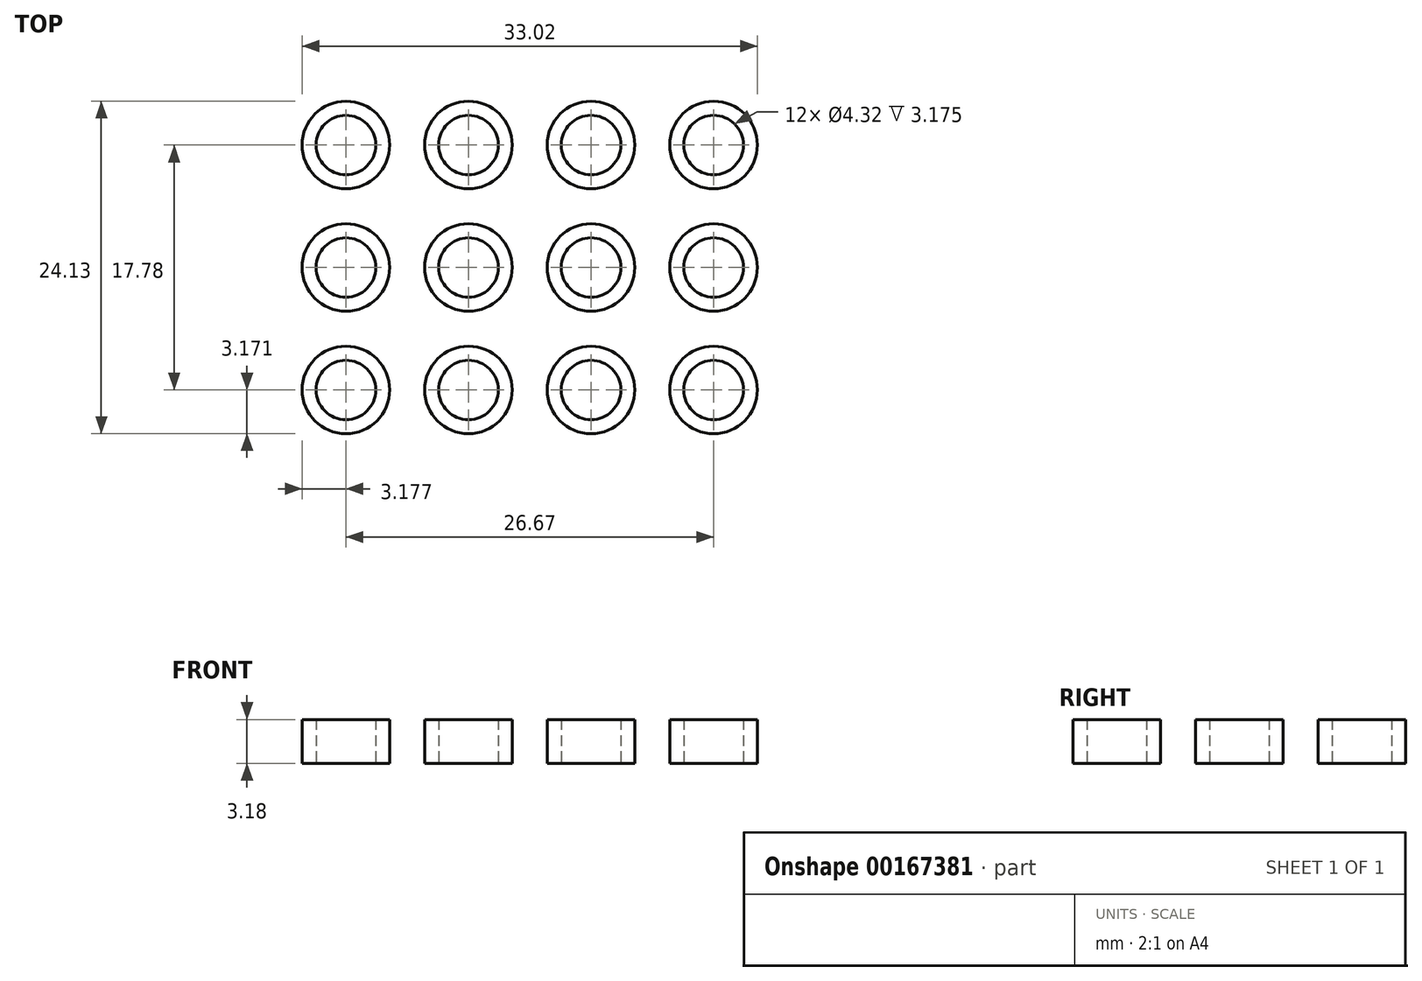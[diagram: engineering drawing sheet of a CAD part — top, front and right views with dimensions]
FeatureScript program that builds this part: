
annotation { "Feature Type Name" : "Feature", "Feature Type Description" : "" }
export const myFeature = defineFeature(function(context is Context, id is Id, definition is map)
    precondition{}
    {
        {
            var Q0;
            Q0=qCreatedBy(makeId("Top.planeOp"),FACE);
            var sketch = newSketch(context, id + "F0", { "sketchPlane" : qUnion([Q0])});
            skCircle(sketch, "E0", {"center": v(25.49, -19.6) * mm, "radius": 2.16 * mm});
            skCircle(sketch, "E1", {"center": v(25.49, -19.6) * mm, "radius": 3.18 * mm});
            skCircle(sketch, "E2", {"center": v(16.6, -19.6) * mm, "radius": 2.16 * mm});
            skCircle(sketch, "E3", {"center": v(16.6, -19.6) * mm, "radius": 3.18 * mm});
            skCircle(sketch, "E4", {"center": v(25.49, -10.7) * mm, "radius": 2.16 * mm});
            skCircle(sketch, "E5", {"center": v(25.49, -10.7) * mm, "radius": 3.18 * mm});
            skCircle(sketch, "E6", {"center": v(16.6, -10.7) * mm, "radius": 2.16 * mm});
            skCircle(sketch, "E7", {"center": v(16.6, -10.7) * mm, "radius": 3.18 * mm});
            skCircle(sketch, "E8", {"center": v(7.7, -10.7) * mm, "radius": 2.16 * mm});
            skCircle(sketch, "E9", {"center": v(7.7, -10.7) * mm, "radius": 3.18 * mm});
            skCircle(sketch, "E10", {"center": v(7.7, -19.6) * mm, "radius": 2.16 * mm});
            skCircle(sketch, "E11", {"center": v(7.7, -19.6) * mm, "radius": 3.18 * mm});
            skCircle(sketch, "E12", {"center": v(7.7, -28.49) * mm, "radius": 2.16 * mm});
            skCircle(sketch, "E13", {"center": v(7.7, -28.49) * mm, "radius": 3.18 * mm});
            skCircle(sketch, "E14", {"center": v(16.6, -28.49) * mm, "radius": 2.16 * mm});
            skCircle(sketch, "E15", {"center": v(16.6, -28.49) * mm, "radius": 3.18 * mm});
            skCircle(sketch, "E16", {"center": v(25.49, -28.49) * mm, "radius": 2.16 * mm});
            skCircle(sketch, "E17", {"center": v(25.49, -28.49) * mm, "radius": 3.18 * mm});
            skCircle(sketch, "E18", {"center": v(34.38, -10.7) * mm, "radius": 2.16 * mm});
            skCircle(sketch, "E19", {"center": v(34.38, -10.7) * mm, "radius": 3.18 * mm});
            skCircle(sketch, "E20", {"center": v(34.38, -19.6) * mm, "radius": 2.16 * mm});
            skCircle(sketch, "E21", {"center": v(34.38, -19.6) * mm, "radius": 3.18 * mm});
            skCircle(sketch, "E22", {"center": v(34.38, -28.49) * mm, "radius": 2.16 * mm});
            skCircle(sketch, "E23", {"center": v(34.38, -28.49) * mm, "radius": 3.18 * mm});
            skSolve(sketch);
        }
        {
            var Q0;
            Q0=qSketchRegion(id+"F0",true);
            extrude(context, id + "F1", {"entities" : qUnion([Q0]), "depth" : 3.17 * mm});
        }
    });
